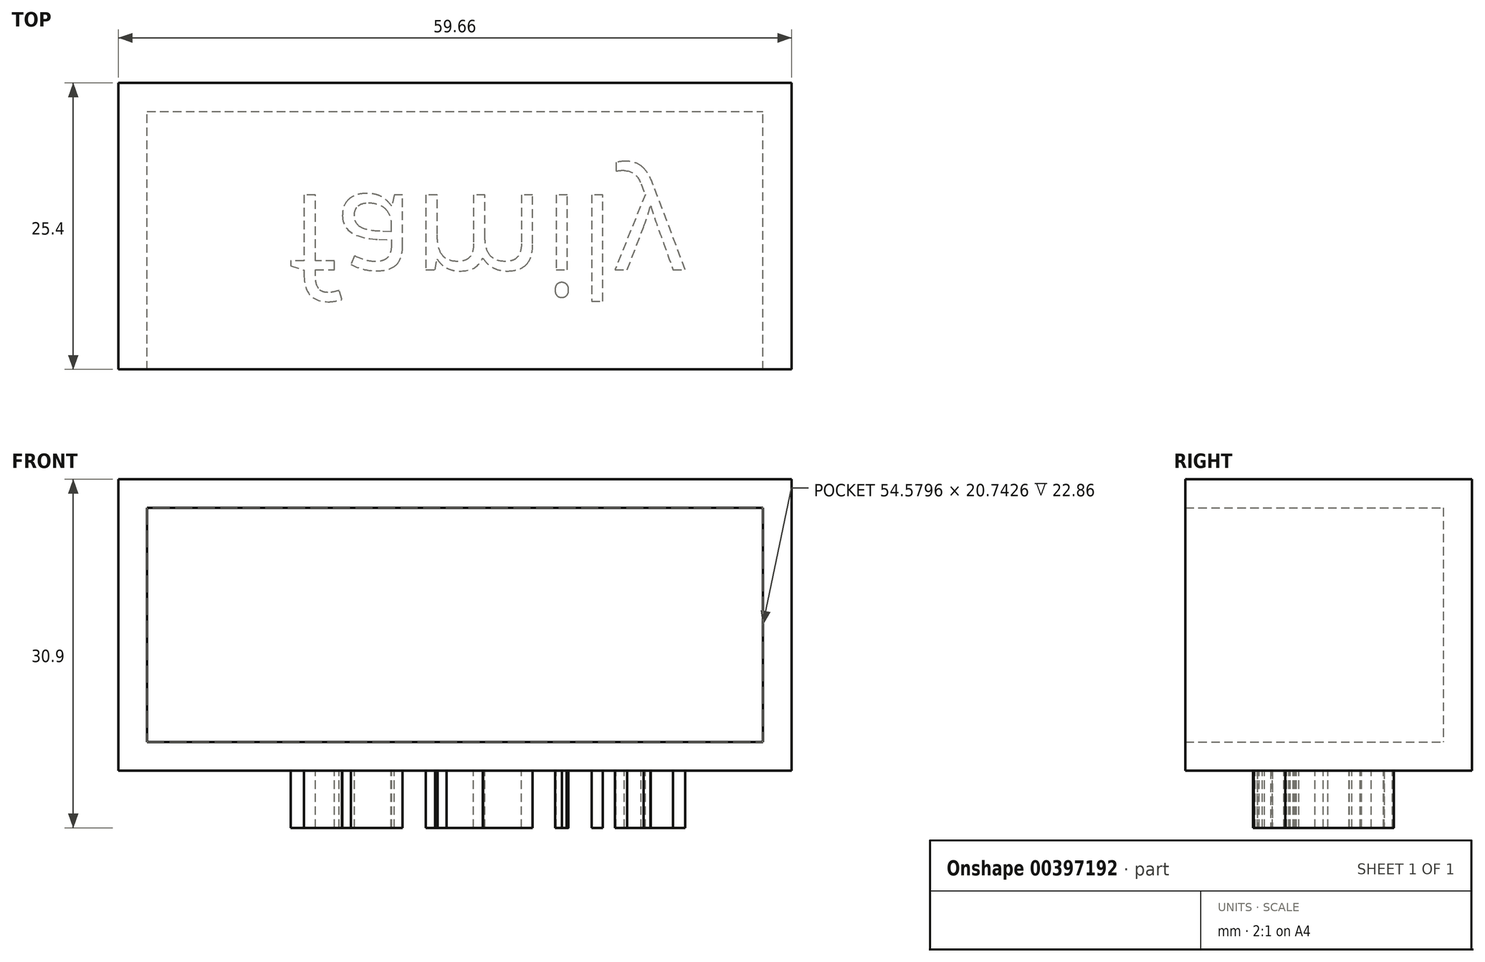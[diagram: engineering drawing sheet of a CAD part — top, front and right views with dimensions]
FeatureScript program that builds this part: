
annotation { "Feature Type Name" : "Feature", "Feature Type Description" : "" }
export const myFeature = defineFeature(function(context is Context, id is Id, definition is map)
    precondition{}
    {
        {
            var Q0;
            Q0=qCreatedBy(makeId("Front.planeOp"),FACE);
            var sketch = newSketch(context, id + "F0", { "sketchPlane" : qUnion([Q0])});
            skLineSegment(sketch, "E0.bottom", {"start": v(0, 0) * mm, "end": v(59.66, 0) * mm});
            skLineSegment(sketch, "E0.top", {"start": v(0, -25.82) * mm, "end": v(59.66, -25.82) * mm});
            skLineSegment(sketch, "E0.left", {"start": v(0, 0) * mm, "end": v(0, -25.82) * mm});
            skLineSegment(sketch, "E0.right", {"start": v(59.66, 0) * mm, "end": v(59.66, -25.82) * mm});
            skSolve(sketch);
        }
        {
            var Q0;
            Q0=makeQuery(id+"F0.imprint","IMPRINT",FACE,{"disambiguationData":[TD([[makeQuery(id+"F0.imprint","IMPRINT",EDGE,{"derivedFrom":sQuery(id+"F0.wireOp",EDGE,"E0.bottom")}),-1.0]])]});
            extrude(context, id + "F1", {"entities" : qUnion([Q0]), "depth" : 25.4 * mm});
        }
        {
            var Q0;
            Q0=makeQuery(id+"F1.opExtrude","CAP_FACE",FACE,{"disambiguationData":[OSD([sQuery(id+"F0.wireOp",EDGE,"E0.bottom"),sQuery(id+"F0.wireOp",EDGE,"E0.top"),sQuery(id+"F0.wireOp",EDGE,"E0.left"),sQuery(id+"F0.wireOp",EDGE,"E0.right")])],"isStart":false});
            shell(context, id + "F2", {"entities" : qUnion([Q0]), "thickness" : 2.54 * mm});
        }
        {
            var Q0;
            Q0=makeQuery(id+"F1.opExtrude","SWEPT_FACE",FACE,{"disambiguationData":[OSD([sQuery(id+"F0.wireOp",EDGE,"E0.top")])]});
            var sketch = newSketch(context, id + "F3", { "sketchPlane" : qUnion([Q0])});
            skText(sketch, "E1", { "text": "family", "fontName": "OpenSans-Regular.ttf"});
            const initialGuessF3  = {"E1": [0.01509, 0.00992, 1, 0, 0.00893]};
            skSetInitialGuess(sketch, initialGuessF3);
            skSolve(sketch);
        }
        {
            var Q0;
            Q0 = qSketchRegion(id + "F3", true);
            extrude(context, id + "F4", {"entities" : qUnion([Q0]), "operationType" : NewBodyOperationType.ADD, "depth" : 5.08 * mm});
        }
    });
